# Revit family: PRD_FrankeWS_WshbsnMnlWtrSpplSts_F3SSelf-closingGateValve_F3SV1003
name_source: partatom
category: Plumbing Fixtures
revit_build: Autodesk Revit 2018 (Build: 20190510_1515(x64)
units: mm (PartAtom-declared; Revit-internal decimal feet)

## family parameters
Cut with Voids When Loaded = Yes
Host = Face
OmniClass Number = 23.45.05.14.99
OmniClass Title = Other Sanitary Washing Plumbing Fixtures
Part Type = Normal
Room Calculation Point = No
Round Connector Dimension = Use Diameter
Shared = No

## types (1)
- F3SV1003
    AdjustableFlowTime = Yes
    AssetType = Fixed
    BIMObjectName = PRD_AR_WashbasinManualWaterSupplySets_F3SSelf-closingGateValve_F3SV1003
    Category = Pr_40_20_87_96, Washbasin manual water supply sets
    CloseOffRating = 0.0 Pa
    Color = Chrome
    Default Elevation = 850 mm  [stored 2.78871 ft]
    Depressurised = No
    Description = F3S self-closing DN 15 shower valve for wall mounting with noise-reducing styrene cladding. Self-closing hydraulically controlled functional part with a piston-free design, and continuously adjustable flow duration. For connection to pre-mixed hot water or cold water. Housing includes shuttle valve position, with interior thread G 1/2, visible parts made of high-polished chrome-plated brass. With rosette, depth adjustability 15 mm.
    DiameterNominal = 15.000 mm
    DurationUnit = year
    Features = For connection to pre-mixed hot water or cold water. Visible parts made of high-polished chrome-plated brass.
    Finish = Polished chrome
    FlowCoefficient = 0
    FlowRateMaximum = 0.05 L/s at 3 bar
    FunctionalPrinciple = Hydraulic self-closing
    GrossWeight = 0.60 kg
    HygieneFlushing = No
    IfcExportAs = IfcValveType
    IfcExportType = USERDEFINED
    InletSize = G-1-2
    Manufacturer = KWC Group AG
    ManufacturerName = KWC Group AG
    ManufacturerURL = www.kwc.com
    Material = Brass
    MaximumFlowTime = 20.00 seconds
    MinimumFlowPressure = 1.00 bar
    MinimumFlowTime = 5.00 seconds
    Model = F3SV1003
    ModelNumber = 2030048760
    ModelReference = F3SV1003
    NBSDescription = Water supply fittings for wash basins and troughs
    NBSReference = 45-35-70/371
    Name = F3S self-closing gate valve F3SV1003
    NetWeight = 0.57 kg
    NominalDepth = 0 mm  [stored 0 ft]
    NominalHeight = 80 mm  [stored 0.262467 ft]
    NominalWidth = 80 mm  [stored 0.262467 ft]
    ProductCode = 208.0587.281
    ProductInformation = https://pim.kwc.com
    ProtectiveShutdown = No
    SoundInsulation = No
    Status = New
    TailorMade = No
    TapMaterial = PRD_AR_ChromatedBrass_HighPolished
    TestPressure = 0.0 Pa
    ThermalDisinfection = No
    TypeOfMixing = No mixing
    TypeOfMounting = In-wall installation without box
    TypeOfOperation = Manual operation
    TypeOfTap = In-wall tap
    URL = www.kwc.com
    Uniclass2015Code = Pr_40_20_87_96
    Uniclass2015Title = Washbasin manual water supply sets
    Uniclass2015Version = Products v1.17
    ValveMechanism = OTHER
    ValveOperation = HYDRAULIC
    ValvePattern = STRAIGHT_2_PORT
    Version = 1
    WarrantyDurationUnit = year
    WorkingPressure = 0.0 Pa

note: [stored X ft] marks values corroborated as IEEE doubles in the binary element streams (Revit-internal decimal feet)

## geometry (parser evidence)
native form markers: Sweep x5
no freeform markers — native parametric forms only
